# Revit family: IS_Edge_A7116_BIM_DE
name_source: partatom
category: Plumbing Fixtures
revit_build: Autodesk Revit 2017 (Build: 20160225_1515(x64)
units: mm (PartAtom-declared; Revit-internal decimal feet)

## family parameters
Always vertical = No
Cut with Voids When Loaded = No
OmniClass Number = 23.45.55.17
OmniClass Title = Mixing Faucets
Part Type = Normal
Room Calculation Point = No
Round Connector Dimension = Use Diameter
Shared = No
Work Plane-Based = No

## types (1)
- A7116AA - EDGE BASIN MXR BIN
    Accessories = http://www.idealstandard.de
    AreaUnits = Millimeter
    AssetType = Fest
    BIMObjectName = ISI_IdealStandard_WashBasinTaps_A7116AA
    BIMobject category = Basins
    BIMobject category code = sanitary-basins
    BIMobject main category = Sanitary
    BIMobject main category code = sanitary
    BOSUseNativeGeometries = 1
    Brand = Ideal Standard
    Brand url = http://www.idealstandard.de
    Color = Chrom
    ConnectionType = Plumbing
    Cost = 0 $
    CurrencyUnit = €
    CurrentRevision = 1
    Date of publishing = 2018_04_13
    Description = EDGE BASIN MXR BIN
    DurationUnit = Jahr
    EAN code = https://4015413343749
    Edition number = 1
    Features = BASIN MXR BIN
    Finish = Chrom
    IFC Classification = Sanitary Terminal
    IfcExportAs = IfcValveType
    IfcExportType = FAUCET
    Installation instructions = http://www.idealstandard.de
    InstallationDate = 1900-12-31T23:59:59
    InstallationInstructions = http://www.idealstandard.de
    LinearUnits = Millimeter
    MainColor = Chrom
    MaintenanceInformation = http://www.idealstandard.de
    Manufacturer name = Ideal Standard
    ManufacturerURL = http://www.idealstandard.de
    Material = Messing
    Material main = Brassware
    Material secondary = Plastic
    Model = A7116AA
    ModelNumber = A7116AA
    ModelReference = EDGE BASIN MXR BIN
    NBS Reference Code = 45-35-70/371
    NBS Reference Description = Water supply fittings for wash basins and troughs
    Name = IdealStandard_WashBasinTaps_A7116AA_ISI
    Nominal height = 102
    Nominal width = 193
    NominalDepth = 209 mm  [stored 0.685696 ft]
    NominalHeight = 102 mm  [stored 0.334646 ft]
    NominalLength = 209 mm  [stored 0.685696 ft]
    NominalWidth = 193 mm  [stored 0.633202 ft]
    Product Guid = ad0f61c4-2497-4b40-b28f-af36db4442aa
    Product SKU = A7116
    Product data url = https://bimobject.com
    Product family = Sanitary
    Product group = Basin mixers
    Product name = EDGE BASIN MXR BIN
    Product url = http://www.idealstandard.de
    ProductInformation = http://www.idealstandard.de
    QR code = http://bimobject.com
    ReplacementCost = 0
    Shape = skulpturiert
    Size = 193 x 209 x 103 mm
    Space = intern
    SpareParts = http://www.idealstandard.de
    Technical description = http://www.idealstandard.de
    TestPressure = 10 Bar
    URL = http://www.idealstandard.de
    Uniclass 2.0 Code = PR-35-79-95
    Uniclass 2.0 Description = Wash Basin And Trough Water Supply Fittings
    Uniclass 2015 Code = Pr_40_20_87_98
    Uniclass 2015 Name = Washbasin taps
    Uniclass2015Code = Pr_40_20_87_98
    Uniclass2015Title = Washbasin taps
    Uniclass2015Version = Products v1.1
    ValveMechanism = Cartridge
    ValveOperation = Lever
    Version = 1
    VolumeUnits = Liter
    WarrantyStartDate = 1900-12-31T23:59:59
    Weight Net (Kg) = 1.6

note: [stored X ft] marks values corroborated as IEEE doubles in the binary element streams (Revit-internal decimal feet)

## geometry (parser evidence)
native form markers: Sweep x1
no freeform markers — native parametric forms only
